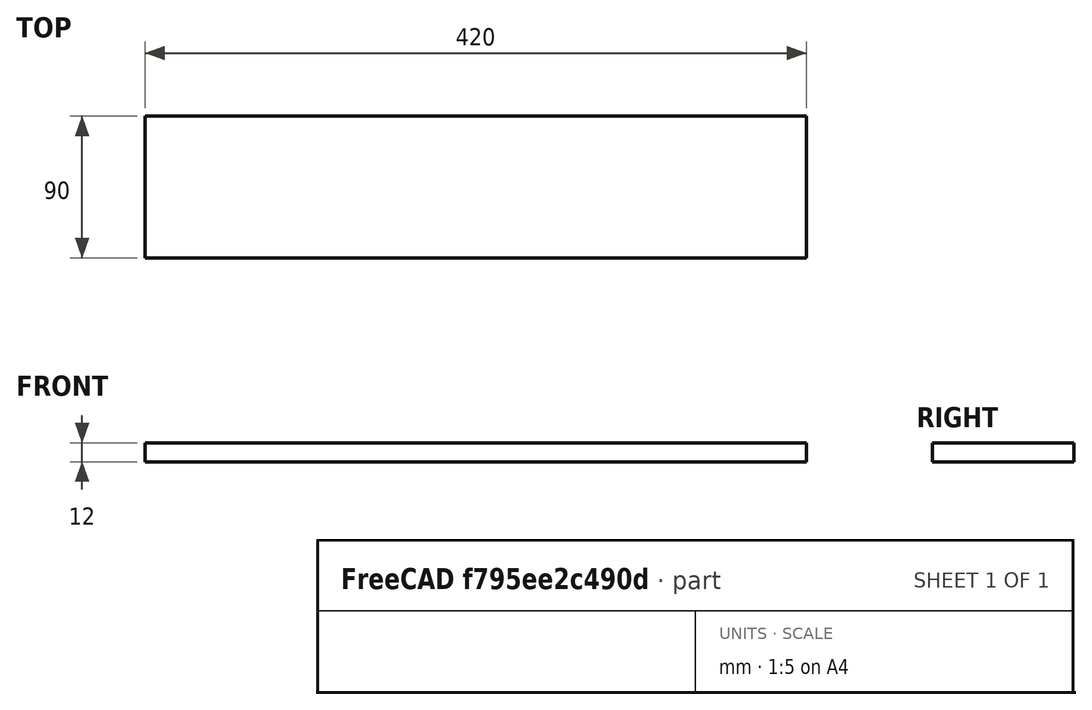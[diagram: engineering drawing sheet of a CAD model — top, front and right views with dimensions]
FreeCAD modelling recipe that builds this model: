
FCSTD DOCUMENT  (FreeCAD 0.18R16131 (Git))
Label: Front_bottom_plate
License: All rights reserved
LicenseURL: http://en.wikipedia.org/wiki/All_rights_reserved
objects: Sketcher::SketchObject×1, PartDesign::Pad×1, PartDesign::Body×1
note: 4 computed .brp shape members not serialized (recipe doc carries the construction recipe); baked Part::Feature solids carry a one-line shape summary decoded from their .brp

FEATURE [Sketcher::SketchObject] Sketch
  MapMode = 5
  Support = -> [XY_Plane]
  sketch-geometry (4):
    g0: LineSegment StartX=0 StartY=0 StartZ=0 EndX=420 EndY=0 EndZ=0
    g1: LineSegment StartX=420 StartY=0 StartZ=0 EndX=420 EndY=90 EndZ=0
    g2: LineSegment StartX=420 StartY=90 StartZ=0 EndX=0 EndY=90 EndZ=0
    g3: LineSegment StartX=0 StartY=90 StartZ=0 EndX=0 EndY=0 EndZ=0
  constraints (11):
    c: Coincident(g0,g1)
    c: Coincident(g1,g2)
    c: Coincident(g2,g3)
    c: Coincident(g3,g0)
    c: Horizontal(g0)
    c: Horizontal(g2)
    c: Vertical(g1)
    c: Vertical(g3)
    c: Coincident(g0,g-1)
    c: DistanceX(g2,g2) = 420
    c: DistanceY(g3,g3) = 90
FEATURE [PartDesign::Pad] Pad
  Length = 12
  Length2 = 100
  Profile = -> Sketch
  Type = 0
FEATURE [PartDesign::Body] Body
  Group = -> [Sketch,Pad]
  Origin = -> Origin
  Tip = -> Pad
